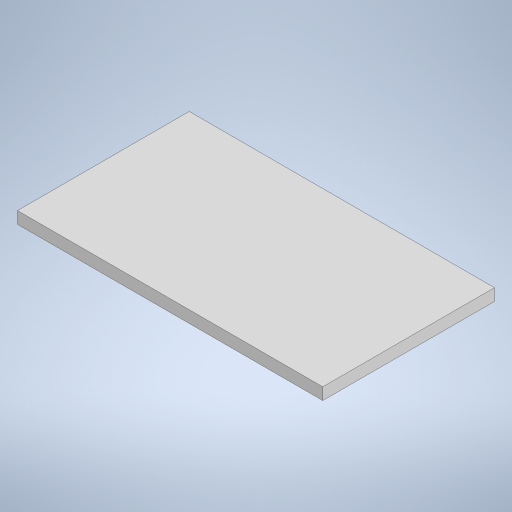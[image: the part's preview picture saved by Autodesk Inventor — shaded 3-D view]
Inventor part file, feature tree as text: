
AUTODESK INVENTOR PART (.ipt)
format: ipt  version: 2024 (Build 280153000, 153)  size: 203,776 bytes
history: native  units: mm
features: extrude x1, sketch x1
ambient origin geometry x8: Origin, YZ Plane, XZ Plane, XY Plane, X Axis, Y Axis, Z Axis, Center Point
bodies: Solid1 (feature_tree)
feature tree (2):
  extrude  "Extrusion1"  Depth=45.0mm
  sketch  "Sketch1"  dims[d0=80.0mm d1=45.0mm d2=3.125mm d3=0.0mm]
